# Revit family: NLRS_57_DUA_UN_round-attenuator-agr-v_LT_sacsr
name_source: partatom
category: Duct Accessories
units: mm (PartAtom-declared; Revit-internal decimal feet)

## family parameters
Always vertical = Yes
Cut with Voids When Loaded = No
Part Type = Breaks Into
Round Connector Dimension = Use Diameter
Shared = No
Work Plane-Based = No

## types (3) — shared parameters
Assembly Code = 57.70
Default Elevation = 2700 mm  [stored 8.85827 ft]
Description = Round sound attenuator
Manufacturer = Solid Air Climate Solutions
Model = Round attenuator
NLRS_C_content_datum_uitgifte = 01-08-2025
NLRS_C_content_provider = Solid Air Climate Systems
NLRS_C_content_versie = Versie 3.22.01
NLRS_C_description = Round sound attenuator
SACS_Data_Hidden = AGR
SACS_Dummy = 1
URL = https://solid-air.nl

## per-type parameters (varying)
| type | SACS_Base_Index |
| AGRYVO | 1 |
| AGRZVO | 2 |
| AGRZVK | 3 |

note: [stored X ft] marks values corroborated as IEEE doubles in the binary element streams (Revit-internal decimal feet)

## geometry (parser evidence)
native form markers: Sweep x5
no freeform markers — native parametric forms only
